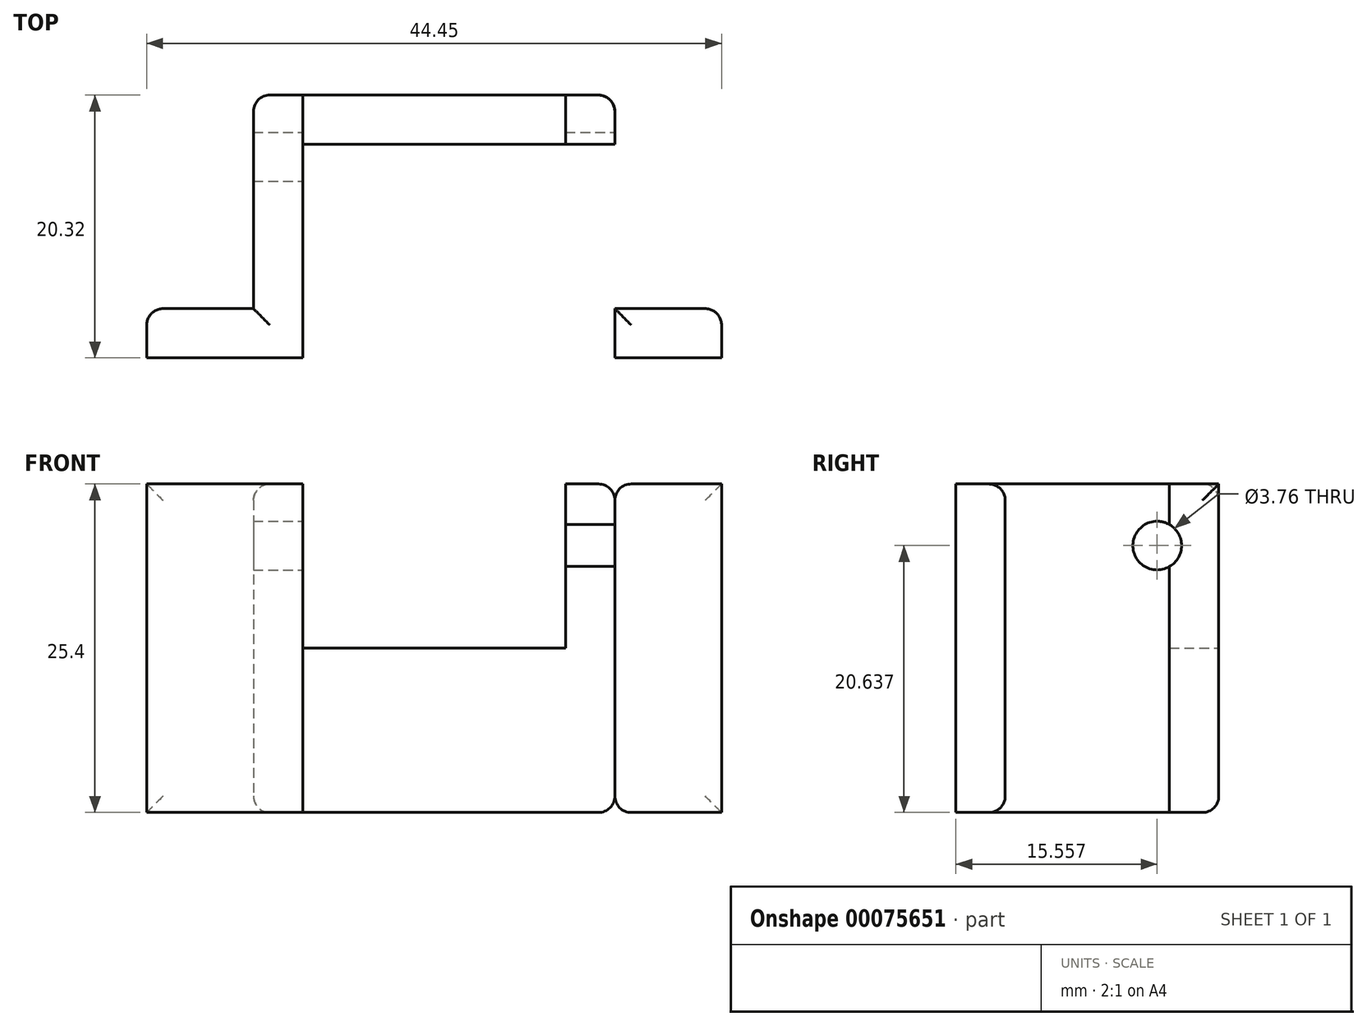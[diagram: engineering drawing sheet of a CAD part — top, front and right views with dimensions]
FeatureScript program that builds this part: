
annotation { "Feature Type Name" : "Feature", "Feature Type Description" : "" }
export const myFeature = defineFeature(function(context is Context, id is Id, definition is map)
    precondition{}
    {
        {
            var Q0;
            Q0=qCreatedBy(makeId("Top.planeOp"),FACE);
            var sketch = newSketch(context, id + "F0", { "sketchPlane" : qUnion([Q0])});
            skLineSegment(sketch, "E0.bottom", {"start": v(0, 0) * mm, "end": v(8.26, 0) * mm});
            skLineSegment(sketch, "E0.top", {"start": v(0, 3.81) * mm, "end": v(8.26, 3.81) * mm});
            skLineSegment(sketch, "E0.left", {"start": v(0, 0) * mm, "end": v(0, 3.81) * mm});
            skLineSegment(sketch, "E0.right", {"start": v(8.26, 0) * mm, "end": v(8.26, 3.81) * mm});
            skLineSegment(sketch, "E1.bottom", {"start": v(8.26, 0) * mm, "end": v(12.07, 0) * mm});
            skLineSegment(sketch, "E1.top", {"start": v(8.26, 16.51) * mm, "end": v(12.06, 16.51) * mm});
            skLineSegment(sketch, "E1.left", {"start": v(8.26, 0) * mm, "end": v(8.25, 16.51) * mm});
            skLineSegment(sketch, "E1.right", {"start": v(12.07, 0) * mm, "end": v(12.06, 16.51) * mm});
            skLineSegment(sketch, "E2.bottom", {"start": v(8.26, 16.51) * mm, "end": v(36.2, 16.51) * mm});
            skLineSegment(sketch, "E2.top", {"start": v(8.26, 20.32) * mm, "end": v(36.2, 20.32) * mm});
            skLineSegment(sketch, "E2.left", {"start": v(8.25, 16.51) * mm, "end": v(8.25, 20.32) * mm});
            skLineSegment(sketch, "E2.right", {"start": v(36.2, 16.51) * mm, "end": v(36.2, 20.32) * mm});
            skLineSegment(sketch, "E3.bottom", {"start": v(36.2, 16.51) * mm, "end": v(32.39, 16.51) * mm});
            skLineSegment(sketch, "E3.top", {"start": v(36.2, 0) * mm, "end": v(32.39, 0) * mm});
            skLineSegment(sketch, "E3.left", {"start": v(36.2, 16.51) * mm, "end": v(36.2, 0) * mm});
            skLineSegment(sketch, "E3.right", {"start": v(32.39, 16.51) * mm, "end": v(32.39, 0) * mm});
            skLineSegment(sketch, "E4.bottom", {"start": v(36.2, 0) * mm, "end": v(44.45, 0) * mm});
            skLineSegment(sketch, "E4.top", {"start": v(36.2, 3.81) * mm, "end": v(44.45, 3.81) * mm});
            skLineSegment(sketch, "E4.left", {"start": v(36.2, 0) * mm, "end": v(36.2, 3.81) * mm});
            skLineSegment(sketch, "E4.right", {"start": v(44.45, 0) * mm, "end": v(44.45, 3.81) * mm});
            skSolve(sketch);
        }
        {
            var Q0;
            {var subQ0=sQuery(id+"F0.wireOp",EDGE,"E0.bottom");Q0=makeQuery(id+"F0.imprint","IMPRINT",FACE,{"disambiguationData":[TD([[makeQuery(id+"F0.imprint","IMPRINT",EDGE,{"derivedFrom":subQ0}),1.0]])]});}
            var Q1;
            {var subQ5=sQuery(id+"F0.wireOp",EDGE,"E1.bottom");Q1=makeQuery(id+"F0.imprint","IMPRINT",FACE,{"disambiguationData":[TD([[makeQuery(id+"F0.imprint","IMPRINT",EDGE,{"derivedFrom":subQ5}),1.0]])]});}
            var Q2;
            Q2=makeQuery(id+"F0.imprint","IMPRINT",FACE,{"disambiguationData":[TD([[makeQuery(id+"F0.imprint","IMPRINT",EDGE,{"derivedFrom":sQuery(id+"F0.wireOp",EDGE,"E2.top")}),-1.0]])]});
            var Q3;
            Q3=makeQuery(id+"F0.imprint","IMPRINT",FACE,{"disambiguationData":[TD([[makeQuery(id+"F0.imprint","IMPRINT",EDGE,{"derivedFrom":sQuery(id+"F0.wireOp",EDGE,"E3.bottom")}),1.0]])]});
            var Q4;
            Q4=makeQuery(id+"F0.imprint","IMPRINT",FACE,{"disambiguationData":[TD([[makeQuery(id+"F0.imprint","IMPRINT",EDGE,{"derivedFrom":sQuery(id+"F0.wireOp",EDGE,"E4.bottom")}),1.0]])]});
            extrude(context, id + "F1", {"entities" : qUnion([Q0, Q1, Q2, Q3, Q4]), "depth" : 25.4 * mm});
        }
        {
            var Q0;
            Q0=makeQuery(id+"F1.opExtrude","CAP_FACE",FACE,{"disambiguationData":[OSD([sQuery(id+"F0.wireOp",EDGE,"E0.bottom"),sQuery(id+"F0.wireOp",EDGE,"E0.top"),sQuery(id+"F0.wireOp",EDGE,"E0.left"),sQuery(id+"F0.wireOp",EDGE,"E1.bottom"),sQuery(id+"F0.wireOp",EDGE,"E1.left"),sQuery(id+"F0.wireOp",EDGE,"E1.right"),sQuery(id+"F0.wireOp",EDGE,"E2.bottom"),sQuery(id+"F0.wireOp",EDGE,"E2.top"),sQuery(id+"F0.wireOp",EDGE,"E2.left"),sQuery(id+"F0.wireOp",EDGE,"E2.right"),sQuery(id+"F0.wireOp",EDGE,"E3.top"),sQuery(id+"F0.wireOp",EDGE,"E3.left"),sQuery(id+"F0.wireOp",EDGE,"E3.right"),sQuery(id+"F0.wireOp",EDGE,"E4.bottom"),sQuery(id+"F0.wireOp",EDGE,"E4.top"),sQuery(id+"F0.wireOp",EDGE,"E4.right")])],"isStart":false});
            var sketch = newSketch(context, id + "F2", { "sketchPlane" : qUnion([Q0])});
            skLineSegment(sketch, "E5.0", {"start": v(8.25, 20.32) * mm, "end": v(36.2, 20.32) * mm});
            skLineSegment(sketch, "E6.0", {"start": v(32.39, 16.51) * mm, "end": v(32.39, 0) * mm});
            skLineSegment(sketch, "E7.0", {"start": v(12.07, 0) * mm, "end": v(12.06, 16.51) * mm});
            skLineSegment(sketch, "E8.bottom", {"start": v(12.06, 16.51) * mm, "end": v(32.39, 16.51) * mm});
            skLineSegment(sketch, "E8.top", {"start": v(12.06, 20.32) * mm, "end": v(32.39, 20.32) * mm});
            skLineSegment(sketch, "E8.left", {"start": v(12.06, 16.51) * mm, "end": v(12.06, 20.32) * mm});
            skLineSegment(sketch, "E8.right", {"start": v(32.39, 16.51) * mm, "end": v(32.39, 20.32) * mm});
            skSolve(sketch);
        }
        {
            var Q0;
            Q0=makeQuery(id+"F2.imprint","IMPRINT",FACE,{"disambiguationData":[TD([[makeQuery(id+"F2.imprint","IMPRINT",EDGE,{"derivedFrom":sQuery(id+"F2.wireOp",EDGE,"E8.bottom")}),1.0]])]});
            extrude(context, id + "F3", {"entities" : qUnion([Q0]), "operationType" : NewBodyOperationType.REMOVE, "oppositeDirection" : true, "depth" : 12.7 * mm});
        }
        {
            var Q0;
            Q0=makeQuery(id+"F1.opExtrude","SWEPT_FACE",FACE,{"disambiguationData":[OSD([sQuery(id+"F0.wireOp",EDGE,"E2.right"),sQuery(id+"F0.wireOp",EDGE,"E3.left")])]});
            var sketch = newSketch(context, id + "F4", { "sketchPlane" : qUnion([Q0])});
            skLineSegment(sketch, "E9.0", {"start": v(3.8, 25.4) * mm, "end": v(20.32, 25.4) * mm});
            skLineSegment(sketch, "E10.0", {"start": v(20.32, 25.4) * mm, "end": v(20.32, 0) * mm});
            skLineSegment(sketch, "E11.0", {"start": v(16.51, 12.7) * mm, "end": v(16.51, 0) * mm});
            skCircle(sketch, "E12", {"center": v(15.56, 20.64) * mm, "radius": 1.88 * mm});
            skSolve(sketch);
        }
        {
            var Q0;
            Q0=makeQuery(id+"F4.imprint","IMPRINT",FACE,{"disambiguationData":[TD([[makeQuery(id+"F4.imprint","IMPRINT",EDGE,{"derivedFrom":sQuery(id+"F4.wireOp",EDGE,"E12")}),1.0]])]});
            extrude(context, id + "F5", {"entities" : qUnion([Q0]), "operationType" : NewBodyOperationType.REMOVE, "endBound" : BoundingType.THROUGH_ALL, "oppositeDirection" : true, "depth" : 25.4 * mm});
        }
        {
            var Q0;
            {var subQ0=sQuery(id+"F0.wireOp",EDGE,"E3.right");var subQ3=sQuery(id+"F0.wireOp",EDGE,"E2.top");Q0=makeQuery(id+"F3.boolean.opBoolean","SPLIT",EDGE,{"disambiguationData":[TD([makeQuery(id+"F1.opExtrude","SWEPT_FACE",FACE,{"disambiguationData":[OSD([subQ0])]})])],"derivedFrom":makeQuery(id+"F1.opExtrude","CAP_EDGE",EDGE,{"disambiguationData":[OSD([subQ3])],"isStart":false})});}
            var Q1;
            {var subQ0=sQuery(id+"F0.wireOp",EDGE,"E2.top");var subQ2=sQuery(id+"F0.wireOp",EDGE,"E1.right");Q1=makeQuery(id+"F3.boolean.opBoolean","SPLIT",EDGE,{"disambiguationData":[TD([makeQuery(id+"F1.opExtrude","SWEPT_FACE",FACE,{"disambiguationData":[OSD([subQ2])]})])],"derivedFrom":makeQuery(id+"F1.opExtrude","CAP_EDGE",EDGE,{"disambiguationData":[OSD([subQ0])],"isStart":false})});}
            var Q2;
            Q2=makeQuery(id+"F1.opExtrude","CAP_EDGE",EDGE,{"disambiguationData":[OSD([sQuery(id+"F0.wireOp",EDGE,"E2.top")])],"isStart":true});
            var Q3;
            Q3=makeQuery(id+"F1.opExtrude","SWEPT_EDGE",EDGE,{"disambiguationData":[OSD([sQuery(id+"F0.wireOp",EDGE,"E2.top"),sQuery(id+"F0.wireOp",EDGE,"E2.right")])]});
            var Q4;
            Q4=makeQuery(id+"F1.opExtrude","SWEPT_EDGE",EDGE,{"disambiguationData":[OSD([sQuery(id+"F0.wireOp",EDGE,"E2.top"),sQuery(id+"F0.wireOp",EDGE,"E2.left")])]});
            var Q5;
            Q5=makeQuery(id+"F1.opExtrude","CAP_EDGE",EDGE,{"disambiguationData":[OSD([sQuery(id+"F0.wireOp",EDGE,"E2.right"),sQuery(id+"F0.wireOp",EDGE,"E3.left")])],"isStart":false});
            var Q6;
            Q6=makeQuery(id+"F1.opExtrude","CAP_EDGE",EDGE,{"disambiguationData":[OSD([sQuery(id+"F0.wireOp",EDGE,"E1.left"),sQuery(id+"F0.wireOp",EDGE,"E2.left")])],"isStart":false});
            var Q7;
            Q7=makeQuery(id+"F1.opExtrude","CAP_EDGE",EDGE,{"disambiguationData":[OSD([sQuery(id+"F0.wireOp",EDGE,"E2.right"),sQuery(id+"F0.wireOp",EDGE,"E3.left")])],"isStart":true});
            var Q8;
            Q8=makeQuery(id+"F1.opExtrude","CAP_EDGE",EDGE,{"disambiguationData":[OSD([sQuery(id+"F0.wireOp",EDGE,"E1.left"),sQuery(id+"F0.wireOp",EDGE,"E2.left")])],"isStart":true});
            var Q9;
            Q9=makeQuery(id+"F1.opExtrude","CAP_EDGE",EDGE,{"disambiguationData":[OSD([sQuery(id+"F0.wireOp",EDGE,"E0.top")])],"isStart":true});
            var Q10;
            Q10=makeQuery(id+"F1.opExtrude","SWEPT_EDGE",EDGE,{"disambiguationData":[OSD([sQuery(id+"F0.wireOp",EDGE,"E0.top"),sQuery(id+"F0.wireOp",EDGE,"E0.left")])]});
            var Q11;
            Q11=makeQuery(id+"F1.opExtrude","CAP_EDGE",EDGE,{"disambiguationData":[OSD([sQuery(id+"F0.wireOp",EDGE,"E0.top")])],"isStart":false});
            var Q12;
            Q12=makeQuery(id+"F1.opExtrude","CAP_EDGE",EDGE,{"disambiguationData":[OSD([sQuery(id+"F0.wireOp",EDGE,"E4.top")])],"isStart":false});
            var Q13;
            Q13=makeQuery(id+"F1.opExtrude","SWEPT_EDGE",EDGE,{"disambiguationData":[OSD([sQuery(id+"F0.wireOp",EDGE,"E4.top"),sQuery(id+"F0.wireOp",EDGE,"E4.right")])]});
            var Q14;
            Q14=makeQuery(id+"F1.opExtrude","CAP_EDGE",EDGE,{"disambiguationData":[OSD([sQuery(id+"F0.wireOp",EDGE,"E4.top")])],"isStart":true});
            fillet(context, id + "F6", {"entities" : qUnion([Q0, Q1, Q2, Q3, Q4, Q5, Q6, Q7, Q8, Q9, Q10, Q11, Q12, Q13, Q14]), "radius" : 1.27 * mm, "tangentPropagation" : true, "allowEdgeOverflow" : false});
        }
    });
